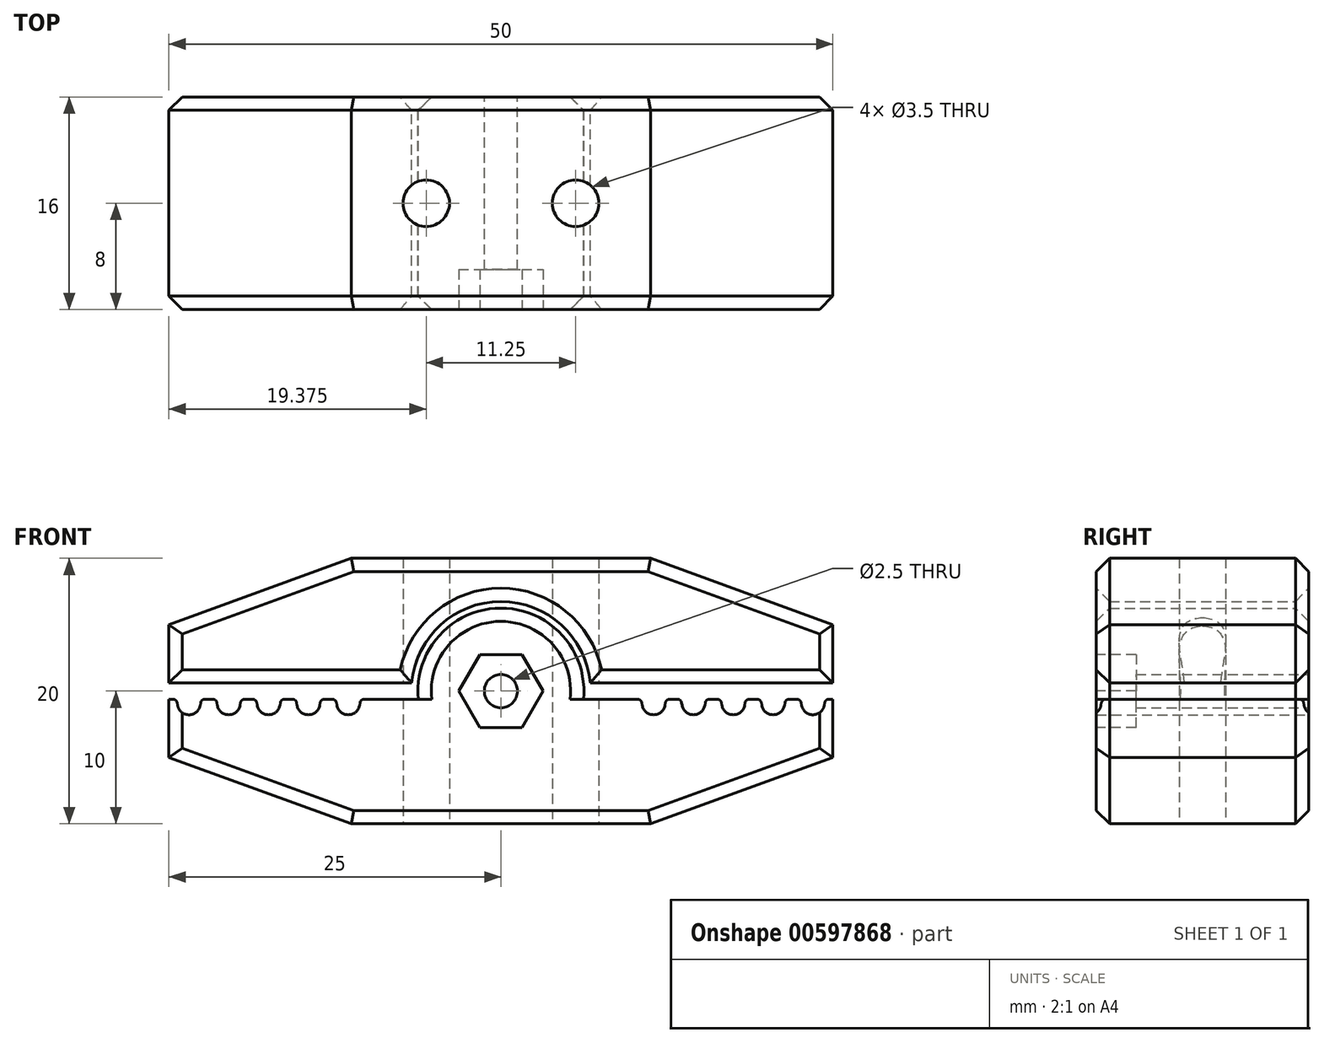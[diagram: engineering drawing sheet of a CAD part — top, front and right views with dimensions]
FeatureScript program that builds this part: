
annotation { "Feature Type Name" : "Feature", "Feature Type Description" : "" }
export const myFeature = defineFeature(function(context is Context, id is Id, definition is map)
    precondition{}
    {
        {
            var Q0;
            Q0=qCreatedBy(makeId("Front.planeOp"),FACE);
            var sketch = newSketch(context, id + "F0", { "sketchPlane" : qUnion([Q0])});
            skCircle(sketch, "E0", {"center": v(0, 0) * mm, "radius": 1.25 * mm});
            skLineSegment(sketch, "E1", {"start": v(0, 0) * mm, "end": v(11.5, 0) * mm, "construction": true});
            skLineSegment(sketch, "E2.bottom", {"start": v(10, 0.62) * mm, "end": v(13, 0.62) * mm});
            skLineSegment(sketch, "E2.left", {"start": v(10, 0.62) * mm, "end": v(10, -0.61) * mm});
            skLineSegment(sketch, "E2.right", {"start": v(13, 0.62) * mm, "end": v(13, -0.61) * mm});
            skPoint(sketch, "E2.middle", {"position": v(11.5, 0) * mm});
            skArc(sketch, "E3", {"start": v(10.64, -1.06) * mm, "mid": v(11.5, -1.78) * mm, "end": v(12.36, -1.06) * mm});
            skPoint(sketch, "E4", {"position": v(11.5, -1.78) * mm});
            skLineSegment(sketch, "E5", {"start": v(10.64, -1.06) * mm, "end": v(10.6, -0.87) * mm});
            skLineSegment(sketch, "E6", {"start": v(11.5, -0.91) * mm, "end": v(11.5, 0.62) * mm, "construction": true});
            skLineSegment(sketch, "E7.MirrorCS", {"start": v(12.36, -1.06) * mm, "end": v(12.39, -0.87) * mm});
            skLineSegment(sketch, "E8", {"start": v(10.31, -0.61) * mm, "end": v(10, -0.61) * mm});
            skLineSegment(sketch, "E9.MirrorCS", {"start": v(12.69, -0.61) * mm, "end": v(13, -0.61) * mm});
            skPoint(sketch, "E10.visualSharp", {"position": v(10.57, -0.61) * mm});
            skArc(sketch, "E10.filletArc", {"start": v(10.6, -0.87) * mm, "mid": v(10.5, -0.69) * mm, "end": v(10.31, -0.61) * mm});
            skPoint(sketch, "E11.visualSharp", {"position": v(12.43, -0.61) * mm});
            skArc(sketch, "E11.filletArc", {"start": v(12.69, -0.61) * mm, "mid": v(12.5, -0.69) * mm, "end": v(12.39, -0.87) * mm});
            skLineSegment(sketch, "E12", {"start": v(10, 0.62) * mm, "end": v(1.25, 0.62) * mm, "construction": true});
            skPoint(sketch, "E13", {"position": v(1.25, 0) * mm});
            skLineSegment(sketch, "E14", {"start": v(5.62, 0.62) * mm, "end": v(5.62, 10) * mm, "construction": true});
            skLineSegment(sketch, "E15.bottom", {"start": v(25, 10) * mm, "end": v(-25, 10) * mm});
            skLineSegment(sketch, "E15.top", {"start": v(25, -10) * mm, "end": v(-25, -10) * mm});
            skLineSegment(sketch, "E15.left", {"start": v(25, 10) * mm, "end": v(25, -10) * mm});
            skLineSegment(sketch, "E15.right", {"start": v(-25, 10) * mm, "end": v(-25, -10) * mm});
            skPoint(sketch, "E16.1.0.0", {"position": v(15.43, -0.61) * mm});
            skLineSegment(sketch, "E16.1.0.1", {"start": v(16, 0.62) * mm, "end": v(16, -0.61) * mm});
            skPoint(sketch, "E16.1.0.2", {"position": v(13.57, -0.61) * mm});
            skLineSegment(sketch, "E16.1.0.4", {"start": v(13, 0.62) * mm, "end": v(16, 0.62) * mm});
            skLineSegment(sketch, "E16.1.0.5", {"start": v(14.5, -0.91) * mm, "end": v(14.5, 0.62) * mm, "construction": true});
            skArc(sketch, "E16.1.0.6", {"start": v(13.64, -1.06) * mm, "mid": v(14.5, -1.78) * mm, "end": v(15.36, -1.06) * mm});
            skPoint(sketch, "E16.1.0.7", {"position": v(14.5, -1.78) * mm});
            skPoint(sketch, "E16.1.0.8", {"position": v(14.5, 0) * mm});
            skPoint(sketch, "E16.1.0.9", {"position": v(15.43, -0.61) * mm});
            skArc(sketch, "E16.1.0.10", {"start": v(13.6, -0.87) * mm, "mid": v(13.5, -0.69) * mm, "end": v(13.31, -0.61) * mm});
            skPoint(sketch, "E16.1.0.11", {"position": v(15.43, -0.61) * mm});
            skLineSegment(sketch, "E16.1.0.12", {"start": v(13.31, -0.61) * mm, "end": v(13, -0.61) * mm});
            skLineSegment(sketch, "E16.1.0.13", {"start": v(13.64, -1.06) * mm, "end": v(13.6, -0.87) * mm});
            skLineSegment(sketch, "E16.1.0.14", {"start": v(15.69, -0.61) * mm, "end": v(16, -0.61) * mm});
            skLineSegment(sketch, "E16.1.0.15", {"start": v(15.69, -0.61) * mm, "end": v(16, -0.61) * mm});
            skLineSegment(sketch, "E16.1.0.16", {"start": v(15.36, -1.06) * mm, "end": v(15.39, -0.87) * mm});
            skArc(sketch, "E16.1.0.17", {"start": v(15.69, -0.61) * mm, "mid": v(15.5, -0.69) * mm, "end": v(15.39, -0.87) * mm});
            skLineSegment(sketch, "E16.1.0.18", {"start": v(15.36, -1.06) * mm, "end": v(15.39, -0.87) * mm});
            skPoint(sketch, "E16.2.0.0", {"position": v(18.43, -0.61) * mm});
            skLineSegment(sketch, "E16.2.0.1", {"start": v(19, 0.62) * mm, "end": v(19, -0.61) * mm});
            skPoint(sketch, "E16.2.0.2", {"position": v(16.57, -0.61) * mm});
            skLineSegment(sketch, "E16.2.0.3", {"start": v(16, 0.62) * mm, "end": v(16, -0.61) * mm});
            skLineSegment(sketch, "E16.2.0.4", {"start": v(16, 0.62) * mm, "end": v(19, 0.62) * mm});
            skLineSegment(sketch, "E16.2.0.5", {"start": v(17.5, -0.91) * mm, "end": v(17.5, 0.62) * mm, "construction": true});
            skArc(sketch, "E16.2.0.6", {"start": v(16.64, -1.06) * mm, "mid": v(17.5, -1.78) * mm, "end": v(18.36, -1.06) * mm});
            skPoint(sketch, "E16.2.0.7", {"position": v(17.5, -1.78) * mm});
            skPoint(sketch, "E16.2.0.8", {"position": v(17.5, 0) * mm});
            skPoint(sketch, "E16.2.0.9", {"position": v(18.43, -0.61) * mm});
            skArc(sketch, "E16.2.0.10", {"start": v(16.6, -0.87) * mm, "mid": v(16.5, -0.69) * mm, "end": v(16.31, -0.61) * mm});
            skPoint(sketch, "E16.2.0.11", {"position": v(18.43, -0.61) * mm});
            skLineSegment(sketch, "E16.2.0.12", {"start": v(16.31, -0.61) * mm, "end": v(16, -0.61) * mm});
            skLineSegment(sketch, "E16.2.0.13", {"start": v(16.64, -1.06) * mm, "end": v(16.6, -0.87) * mm});
            skLineSegment(sketch, "E16.2.0.14", {"start": v(18.69, -0.61) * mm, "end": v(19, -0.61) * mm});
            skLineSegment(sketch, "E16.2.0.15", {"start": v(18.69, -0.61) * mm, "end": v(19, -0.61) * mm});
            skLineSegment(sketch, "E16.2.0.16", {"start": v(18.36, -1.06) * mm, "end": v(18.39, -0.87) * mm});
            skArc(sketch, "E16.2.0.17", {"start": v(18.69, -0.61) * mm, "mid": v(18.5, -0.69) * mm, "end": v(18.39, -0.87) * mm});
            skLineSegment(sketch, "E16.2.0.18", {"start": v(18.36, -1.06) * mm, "end": v(18.39, -0.87) * mm});
            skPoint(sketch, "E16.3.0.0", {"position": v(21.43, -0.61) * mm});
            skLineSegment(sketch, "E16.3.0.1", {"start": v(22, 0.62) * mm, "end": v(22, -0.61) * mm});
            skPoint(sketch, "E16.3.0.2", {"position": v(19.57, -0.61) * mm});
            skLineSegment(sketch, "E16.3.0.3", {"start": v(19, 0.62) * mm, "end": v(19, -0.61) * mm});
            skLineSegment(sketch, "E16.3.0.4", {"start": v(19, 0.62) * mm, "end": v(22, 0.62) * mm});
            skLineSegment(sketch, "E16.3.0.5", {"start": v(20.5, -0.91) * mm, "end": v(20.5, 0.62) * mm, "construction": true});
            skArc(sketch, "E16.3.0.6", {"start": v(19.64, -1.06) * mm, "mid": v(20.5, -1.78) * mm, "end": v(21.36, -1.06) * mm});
            skPoint(sketch, "E16.3.0.7", {"position": v(20.5, -1.78) * mm});
            skPoint(sketch, "E16.3.0.8", {"position": v(20.5, 0) * mm});
            skPoint(sketch, "E16.3.0.9", {"position": v(21.43, -0.61) * mm});
            skArc(sketch, "E16.3.0.10", {"start": v(19.6, -0.87) * mm, "mid": v(19.5, -0.69) * mm, "end": v(19.31, -0.61) * mm});
            skPoint(sketch, "E16.3.0.11", {"position": v(21.43, -0.61) * mm});
            skLineSegment(sketch, "E16.3.0.12", {"start": v(19.31, -0.61) * mm, "end": v(19, -0.61) * mm});
            skLineSegment(sketch, "E16.3.0.13", {"start": v(19.64, -1.06) * mm, "end": v(19.6, -0.87) * mm});
            skLineSegment(sketch, "E16.3.0.14", {"start": v(21.69, -0.61) * mm, "end": v(22, -0.61) * mm});
            skLineSegment(sketch, "E16.3.0.15", {"start": v(21.69, -0.61) * mm, "end": v(22, -0.61) * mm});
            skLineSegment(sketch, "E16.3.0.16", {"start": v(21.36, -1.06) * mm, "end": v(21.39, -0.87) * mm});
            skArc(sketch, "E16.3.0.17", {"start": v(21.69, -0.61) * mm, "mid": v(21.5, -0.69) * mm, "end": v(21.39, -0.87) * mm});
            skLineSegment(sketch, "E16.3.0.18", {"start": v(21.36, -1.06) * mm, "end": v(21.39, -0.87) * mm});
            skPoint(sketch, "E16.4.0.0", {"position": v(24.43, -0.61) * mm});
            skLineSegment(sketch, "E16.4.0.1", {"start": v(25, 0.62) * mm, "end": v(25, -0.61) * mm});
            skPoint(sketch, "E16.4.0.2", {"position": v(22.57, -0.61) * mm});
            skLineSegment(sketch, "E16.4.0.3", {"start": v(22, 0.62) * mm, "end": v(22, -0.61) * mm});
            skLineSegment(sketch, "E16.4.0.4", {"start": v(22, 0.62) * mm, "end": v(25, 0.62) * mm});
            skLineSegment(sketch, "E16.4.0.5", {"start": v(23.5, -0.91) * mm, "end": v(23.5, 0.62) * mm, "construction": true});
            skArc(sketch, "E16.4.0.6", {"start": v(22.64, -1.06) * mm, "mid": v(23.5, -1.78) * mm, "end": v(24.36, -1.06) * mm});
            skPoint(sketch, "E16.4.0.7", {"position": v(23.5, -1.78) * mm});
            skPoint(sketch, "E16.4.0.8", {"position": v(23.5, 0) * mm});
            skPoint(sketch, "E16.4.0.9", {"position": v(24.43, -0.61) * mm});
            skArc(sketch, "E16.4.0.10", {"start": v(22.6, -0.87) * mm, "mid": v(22.5, -0.69) * mm, "end": v(22.31, -0.61) * mm});
            skPoint(sketch, "E16.4.0.11", {"position": v(24.43, -0.61) * mm});
            skLineSegment(sketch, "E16.4.0.12", {"start": v(22.31, -0.61) * mm, "end": v(22, -0.61) * mm});
            skLineSegment(sketch, "E16.4.0.13", {"start": v(22.64, -1.06) * mm, "end": v(22.6, -0.87) * mm});
            skLineSegment(sketch, "E16.4.0.14", {"start": v(24.69, -0.61) * mm, "end": v(25, -0.61) * mm});
            skLineSegment(sketch, "E16.4.0.15", {"start": v(24.69, -0.61) * mm, "end": v(25, -0.61) * mm});
            skLineSegment(sketch, "E16.4.0.16", {"start": v(24.36, -1.06) * mm, "end": v(24.39, -0.87) * mm});
            skArc(sketch, "E16.4.0.17", {"start": v(24.69, -0.61) * mm, "mid": v(24.5, -0.69) * mm, "end": v(24.39, -0.87) * mm});
            skLineSegment(sketch, "E16.4.0.18", {"start": v(24.36, -1.06) * mm, "end": v(24.39, -0.87) * mm});
            skLineSegment(sketch, "E16.direction1", {"start": v(10, -0.61) * mm, "end": v(13, -0.61) * mm, "construction": true});
            skArc(sketch, "E17", {"start": v(6.22, -0.61) * mm, "mid": v(-4.2, 4.63) * mm, "end": v(0, -6.25) * mm});
            skPoint(sketch, "E18", {"position": v(6.25, 0) * mm});
            skLineSegment(sketch, "E19", {"start": v(10, -0.61) * mm, "end": v(6.22, -0.61) * mm});
            skLineSegment(sketch, "E20", {"start": v(10, 0.62) * mm, "end": v(6.22, 0.62) * mm});
            skPoint(sketch, "E21", {"position": v(0, 6.25) * mm});
            skPoint(sketch, "E21.positionSnap0", {"position": v(0, 10) * mm});
            skLineSegment(sketch, "E22", {"start": v(0, 0) * mm, "end": v(0, 10) * mm, "construction": true});
            skArc(sketch, "E23", {"start": v(6.72, -0.61) * mm, "mid": v(-4.55, 4.99) * mm, "end": v(0, -6.75) * mm});
            skLineSegment(sketch, "E24", {"start": v(0, 10) * mm, "end": v(0, -10) * mm});
            skLineSegment(sketch, "E25", {"start": v(25, -5) * mm, "end": v(11.26, -10) * mm});
            skLineSegment(sketch, "E26.MirrorCS", {"start": v(25, 5) * mm, "end": v(11.26, 10) * mm});
            skSolve(sketch);
        }
        {
            var Q0;
            Q0=makeQuery(id+"F0.imprint","IMPRINT",FACE,{"disambiguationData":[TD([[makeQuery(id+"F0.imprint","IMPRINT",EDGE,{"derivedFrom":sQuery(id+"F0.wireOp",EDGE,"E3")}),-1.0]])]});
            extrude(context, id + "F1", {"entities" : qUnion([Q0]), "depth" : 16 * mm, "offsetDistance" : 25 * mm});
        }
        {
            var Q0;
            {var subQ6=sQuery(id+"F0.wireOp",EDGE,"E2.bottom");Q0=makeQuery(id+"F0.imprint","IMPRINT",FACE,{"disambiguationData":[TD([[makeQuery(id+"F0.imprint","IMPRINT",EDGE,{"derivedFrom":subQ6}),1.0]])]});}
            extrude(context, id + "F2", {"entities" : qUnion([Q0]), "depth" : 16 * mm, "offsetDistance" : 25 * mm});
        }
        {
            var Q0;
            Q0=makeQuery(id+"F1.opExtrude","SWEPT_FACE",FACE,{"disambiguationData":[OSD([sQuery(id+"F0.wireOp",EDGE,"E15.top")])]});
            var sketch = newSketch(context, id + "F3", { "sketchPlane" : qUnion([Q0])});
            skLineSegment(sketch, "E27", {"start": v(5.62, 0) * mm, "end": v(5.62, 16) * mm, "construction": true});
            skCircle(sketch, "E28", {"center": v(5.62, 8) * mm, "radius": 1.75 * mm});
            skSolve(sketch);
        }
        {
            var Q0;
            Q0=qSketchRegion(id+"F3",true);
            extrude(context, id + "F4", {"entities" : qUnion([Q0]), "operationType" : NewBodyOperationType.REMOVE, "endBound" : BoundingType.THROUGH_ALL, "oppositeDirection" : true, "depth" : 25 * mm, "offsetDistance" : 25 * mm});
        }
        {
            var Q0;
            Q0=makeQuery(id+"F1.opExtrude","SWEPT_BODY",BODY,{"disambiguationData":[OSD([sQuery(id+"F0.wireOp",EDGE,"E0"),sQuery(id+"F0.wireOp",EDGE,"E3"),sQuery(id+"F0.wireOp",EDGE,"E5"),sQuery(id+"F0.wireOp",EDGE,"E7.MirrorCS"),sQuery(id+"F0.wireOp",EDGE,"E8"),sQuery(id+"F0.wireOp",EDGE,"E9.MirrorCS"),sQuery(id+"F0.wireOp",EDGE,"E10.filletArc"),sQuery(id+"F0.wireOp",EDGE,"E11.filletArc"),sQuery(id+"F0.wireOp",EDGE,"E15.top"),sQuery(id+"F0.wireOp",EDGE,"E15.left"),sQuery(id+"F0.wireOp",EDGE,"E16.1.0.6"),sQuery(id+"F0.wireOp",EDGE,"E16.1.0.10"),sQuery(id+"F0.wireOp",EDGE,"E16.1.0.12"),sQuery(id+"F0.wireOp",EDGE,"E16.1.0.13"),sQuery(id+"F0.wireOp",EDGE,"E16.1.0.15"),sQuery(id+"F0.wireOp",EDGE,"E16.1.0.17"),sQuery(id+"F0.wireOp",EDGE,"E16.1.0.18"),sQuery(id+"F0.wireOp",EDGE,"E16.2.0.6"),sQuery(id+"F0.wireOp",EDGE,"E16.2.0.10"),sQuery(id+"F0.wireOp",EDGE,"E16.2.0.12"),sQuery(id+"F0.wireOp",EDGE,"E16.2.0.13"),sQuery(id+"F0.wireOp",EDGE,"E16.2.0.15"),sQuery(id+"F0.wireOp",EDGE,"E16.2.0.17"),sQuery(id+"F0.wireOp",EDGE,"E16.2.0.18"),sQuery(id+"F0.wireOp",EDGE,"E16.3.0.6"),sQuery(id+"F0.wireOp",EDGE,"E16.3.0.10"),sQuery(id+"F0.wireOp",EDGE,"E16.3.0.12"),sQuery(id+"F0.wireOp",EDGE,"E16.3.0.13"),sQuery(id+"F0.wireOp",EDGE,"E16.3.0.15"),sQuery(id+"F0.wireOp",EDGE,"E16.3.0.17"),sQuery(id+"F0.wireOp",EDGE,"E16.3.0.18"),sQuery(id+"F0.wireOp",EDGE,"E16.4.0.6"),sQuery(id+"F0.wireOp",EDGE,"E16.4.0.10"),sQuery(id+"F0.wireOp",EDGE,"E16.4.0.12"),sQuery(id+"F0.wireOp",EDGE,"E16.4.0.13"),sQuery(id+"F0.wireOp",EDGE,"E16.4.0.15"),sQuery(id+"F0.wireOp",EDGE,"E16.4.0.17"),sQuery(id+"F0.wireOp",EDGE,"E16.4.0.18"),sQuery(id+"F0.wireOp",EDGE,"E17"),sQuery(id+"F0.wireOp",EDGE,"E19"),sQuery(id+"F0.wireOp",EDGE,"E24"),sQuery(id+"F0.wireOp",EDGE,"E25")])]});
            var Q1;
            Q1=makeQuery(id+"F2.opExtrude","SWEPT_BODY",BODY,{"disambiguationData":[OSD([sQuery(id+"F0.wireOp",EDGE,"E2.bottom"),sQuery(id+"F0.wireOp",EDGE,"E15.bottom"),sQuery(id+"F0.wireOp",EDGE,"E15.left"),sQuery(id+"F0.wireOp",EDGE,"E16.1.0.4"),sQuery(id+"F0.wireOp",EDGE,"E16.2.0.4"),sQuery(id+"F0.wireOp",EDGE,"E16.3.0.4"),sQuery(id+"F0.wireOp",EDGE,"E16.4.0.4"),sQuery(id+"F0.wireOp",EDGE,"E20"),sQuery(id+"F0.wireOp",EDGE,"E23"),sQuery(id+"F0.wireOp",EDGE,"E24"),sQuery(id+"F0.wireOp",EDGE,"E26.MirrorCS")])]});
            var Q2;
            Q2=qCreatedBy(makeId("Right.planeOp"),FACE);
            mirror(context, id + "F5", {"operationType" : NewBodyOperationType.ADD, "entities" : qUnion([Q0, Q1]), "mirrorPlane" : qUnion([Q2])});
        }
        {
            var Q0;
            {var subQ0=makeQuery(id+"F2.opExtrude","CAP_FACE",FACE,{"disambiguationData":[OSD([sQuery(id+"F0.wireOp",EDGE,"E2.bottom"),sQuery(id+"F0.wireOp",EDGE,"E15.bottom"),sQuery(id+"F0.wireOp",EDGE,"E15.left"),sQuery(id+"F0.wireOp",EDGE,"E16.1.0.4"),sQuery(id+"F0.wireOp",EDGE,"E16.2.0.4"),sQuery(id+"F0.wireOp",EDGE,"E16.3.0.4"),sQuery(id+"F0.wireOp",EDGE,"E16.4.0.4"),sQuery(id+"F0.wireOp",EDGE,"E20"),sQuery(id+"F0.wireOp",EDGE,"E23"),sQuery(id+"F0.wireOp",EDGE,"E24"),sQuery(id+"F0.wireOp",EDGE,"E26.MirrorCS")])],"isStart":false});Q0=makeQuery(id+"F5.boolean.opBoolean","MERGE",FACE,{"derivedFrom":[subQ0,makeQuery(id+"F5.opPattern","COPY",FACE,{"derivedFrom":subQ0,"instanceName":"1"})]});}
            var Q1;
            {var subQ0=makeQuery(id+"F2.opExtrude","CAP_FACE",FACE,{"disambiguationData":[OSD([sQuery(id+"F0.wireOp",EDGE,"E2.bottom"),sQuery(id+"F0.wireOp",EDGE,"E15.bottom"),sQuery(id+"F0.wireOp",EDGE,"E15.left"),sQuery(id+"F0.wireOp",EDGE,"E16.1.0.4"),sQuery(id+"F0.wireOp",EDGE,"E16.2.0.4"),sQuery(id+"F0.wireOp",EDGE,"E16.3.0.4"),sQuery(id+"F0.wireOp",EDGE,"E16.4.0.4"),sQuery(id+"F0.wireOp",EDGE,"E20"),sQuery(id+"F0.wireOp",EDGE,"E23"),sQuery(id+"F0.wireOp",EDGE,"E24"),sQuery(id+"F0.wireOp",EDGE,"E26.MirrorCS")])],"isStart":true});Q1=makeQuery(id+"F5.boolean.opBoolean","MERGE",FACE,{"derivedFrom":[subQ0,makeQuery(id+"F5.opPattern","COPY",FACE,{"derivedFrom":subQ0,"instanceName":"1"})]});}
            var Q2;
            Q2=makeQuery(id+"F5.opPattern","COPY",EDGE,{"derivedFrom":makeQuery(id+"F1.opExtrude","CAP_EDGE",EDGE,{"disambiguationData":[OSD([sQuery(id+"F0.wireOp",EDGE,"E25")])],"isStart":false}),"instanceName":"1"});
            var Q3;
            Q3=makeQuery(id+"F1.opExtrude","CAP_EDGE",EDGE,{"disambiguationData":[OSD([sQuery(id+"F0.wireOp",EDGE,"E25")])],"isStart":false});
            var Q4;
            {var subQ0=makeQuery(id+"F1.opExtrude","CAP_EDGE",EDGE,{"disambiguationData":[OSD([sQuery(id+"F0.wireOp",EDGE,"E15.top")])],"isStart":false});Q4=makeQuery(id+"F5.boolean.opBoolean","MERGE",EDGE,{"derivedFrom":[subQ0,makeQuery(id+"F5.opPattern","COPY",EDGE,{"derivedFrom":subQ0,"instanceName":"1"})]});}
            var Q5;
            Q5=makeQuery(id+"F5.opPattern","COPY",EDGE,{"derivedFrom":makeQuery(id+"F1.opExtrude","CAP_EDGE",EDGE,{"disambiguationData":[OSD([sQuery(id+"F0.wireOp",EDGE,"E25")])],"isStart":true}),"instanceName":"1"});
            var Q6;
            {var subQ0=makeQuery(id+"F1.opExtrude","CAP_EDGE",EDGE,{"disambiguationData":[OSD([sQuery(id+"F0.wireOp",EDGE,"E15.top")])],"isStart":true});Q6=makeQuery(id+"F5.boolean.opBoolean","MERGE",EDGE,{"derivedFrom":[subQ0,makeQuery(id+"F5.opPattern","COPY",EDGE,{"derivedFrom":subQ0,"instanceName":"1"})]});}
            var Q7;
            Q7=makeQuery(id+"F1.opExtrude","CAP_EDGE",EDGE,{"disambiguationData":[OSD([sQuery(id+"F0.wireOp",EDGE,"E25")])],"isStart":true});
            var Q8;
            Q8=makeQuery(id+"F5.opPattern","COPY",EDGE,{"derivedFrom":makeQuery(id+"F1.opExtrude","CAP_EDGE",EDGE,{"disambiguationData":[OSD([sQuery(id+"F0.wireOp",EDGE,"E15.left")])],"isStart":false}),"instanceName":"1"});
            var Q9;
            Q9=makeQuery(id+"F1.opExtrude","CAP_EDGE",EDGE,{"disambiguationData":[OSD([sQuery(id+"F0.wireOp",EDGE,"E15.left")])],"isStart":false});
            var Q10;
            Q10=makeQuery(id+"F1.opExtrude","CAP_EDGE",EDGE,{"disambiguationData":[OSD([sQuery(id+"F0.wireOp",EDGE,"E15.left")])],"isStart":true});
            var Q11;
            Q11=makeQuery(id+"F5.opPattern","COPY",EDGE,{"derivedFrom":makeQuery(id+"F1.opExtrude","CAP_EDGE",EDGE,{"disambiguationData":[OSD([sQuery(id+"F0.wireOp",EDGE,"E15.left")])],"isStart":true}),"instanceName":"1"});
            var Q12;
            {var subQ0=makeQuery(id+"F1.opExtrude","CAP_EDGE",EDGE,{"disambiguationData":[OSD([sQuery(id+"F0.wireOp",EDGE,"E17")])],"isStart":true});Q12=makeQuery(id+"F5.boolean.opBoolean","MERGE",EDGE,{"derivedFrom":[subQ0,makeQuery(id+"F5.opPattern","COPY",EDGE,{"derivedFrom":subQ0,"instanceName":"1"})]});}
            var Q13;
            {var subQ0=makeQuery(id+"F1.opExtrude","CAP_EDGE",EDGE,{"disambiguationData":[OSD([sQuery(id+"F0.wireOp",EDGE,"E17")])],"isStart":false});Q13=makeQuery(id+"F5.boolean.opBoolean","MERGE",EDGE,{"derivedFrom":[subQ0,makeQuery(id+"F5.opPattern","COPY",EDGE,{"derivedFrom":subQ0,"instanceName":"1"})]});}
            chamfer(context, id + "F6", {"entities" : qUnion([Q0, Q1, Q2, Q3, Q4, Q5, Q6, Q7, Q8, Q9, Q10, Q11, Q12, Q13]), "width" : 1 * mm, "tangentPropagation" : true});
        }
        {
            var Q0;
            {var subQ0=makeQuery(id+"F1.opExtrude","CAP_FACE",FACE,{"disambiguationData":[OSD([sQuery(id+"F0.wireOp",EDGE,"E0"),sQuery(id+"F0.wireOp",EDGE,"E3"),sQuery(id+"F0.wireOp",EDGE,"E5"),sQuery(id+"F0.wireOp",EDGE,"E7.MirrorCS"),sQuery(id+"F0.wireOp",EDGE,"E8"),sQuery(id+"F0.wireOp",EDGE,"E9.MirrorCS"),sQuery(id+"F0.wireOp",EDGE,"E10.filletArc"),sQuery(id+"F0.wireOp",EDGE,"E11.filletArc"),sQuery(id+"F0.wireOp",EDGE,"E15.top"),sQuery(id+"F0.wireOp",EDGE,"E15.left"),sQuery(id+"F0.wireOp",EDGE,"E16.1.0.6"),sQuery(id+"F0.wireOp",EDGE,"E16.1.0.10"),sQuery(id+"F0.wireOp",EDGE,"E16.1.0.12"),sQuery(id+"F0.wireOp",EDGE,"E16.1.0.13"),sQuery(id+"F0.wireOp",EDGE,"E16.1.0.15"),sQuery(id+"F0.wireOp",EDGE,"E16.1.0.17"),sQuery(id+"F0.wireOp",EDGE,"E16.1.0.18"),sQuery(id+"F0.wireOp",EDGE,"E16.2.0.6"),sQuery(id+"F0.wireOp",EDGE,"E16.2.0.10"),sQuery(id+"F0.wireOp",EDGE,"E16.2.0.12"),sQuery(id+"F0.wireOp",EDGE,"E16.2.0.13"),sQuery(id+"F0.wireOp",EDGE,"E16.2.0.15"),sQuery(id+"F0.wireOp",EDGE,"E16.2.0.17"),sQuery(id+"F0.wireOp",EDGE,"E16.2.0.18"),sQuery(id+"F0.wireOp",EDGE,"E16.3.0.6"),sQuery(id+"F0.wireOp",EDGE,"E16.3.0.10"),sQuery(id+"F0.wireOp",EDGE,"E16.3.0.12"),sQuery(id+"F0.wireOp",EDGE,"E16.3.0.13"),sQuery(id+"F0.wireOp",EDGE,"E16.3.0.15"),sQuery(id+"F0.wireOp",EDGE,"E16.3.0.17"),sQuery(id+"F0.wireOp",EDGE,"E16.3.0.18"),sQuery(id+"F0.wireOp",EDGE,"E16.4.0.6"),sQuery(id+"F0.wireOp",EDGE,"E16.4.0.10"),sQuery(id+"F0.wireOp",EDGE,"E16.4.0.12"),sQuery(id+"F0.wireOp",EDGE,"E16.4.0.13"),sQuery(id+"F0.wireOp",EDGE,"E16.4.0.15"),sQuery(id+"F0.wireOp",EDGE,"E16.4.0.17"),sQuery(id+"F0.wireOp",EDGE,"E16.4.0.18"),sQuery(id+"F0.wireOp",EDGE,"E17"),sQuery(id+"F0.wireOp",EDGE,"E19"),sQuery(id+"F0.wireOp",EDGE,"E24"),sQuery(id+"F0.wireOp",EDGE,"E25")])],"isStart":false});Q0=makeQuery(id+"F5.boolean.opBoolean","MERGE",FACE,{"derivedFrom":[subQ0,makeQuery(id+"F5.opPattern","COPY",FACE,{"derivedFrom":subQ0,"instanceName":"1"})]});}
            var sketch = newSketch(context, id + "F7", { "sketchPlane" : qUnion([Q0])});
            skCircle(sketch, "E29.cCircle", {"center": v(0, 0) * mm, "radius": 2.75 * mm, "construction": true});
            skLineSegment(sketch, "E29.0", {"start": v(1.59, 2.75) * mm, "end": v(3.18, 0) * mm});
            skLineSegment(sketch, "E29.1", {"start": v(3.18, 0) * mm, "end": v(1.59, -2.75) * mm});
            skLineSegment(sketch, "E29.2", {"start": v(1.59, -2.75) * mm, "end": v(-1.59, -2.75) * mm});
            skLineSegment(sketch, "E29.3", {"start": v(-1.59, -2.75) * mm, "end": v(-3.18, 0) * mm});
            skLineSegment(sketch, "E29.4", {"start": v(-3.18, 0) * mm, "end": v(-1.59, 2.75) * mm});
            skLineSegment(sketch, "E29.5", {"start": v(-1.59, 2.75) * mm, "end": v(1.59, 2.75) * mm});
            skPoint(sketch, "E29.0.midPoint", {"position": v(2.38, 1.38) * mm});
            skSolve(sketch);
        }
        {
            var Q0;
            Q0=qSketchRegion(id+"F7",true);
            extrude(context, id + "F8", {"entities" : qUnion([Q0]), "operationType" : NewBodyOperationType.REMOVE, "oppositeDirection" : true, "depth" : 3 * mm, "offsetDistance" : 25 * mm});
        }
    });
